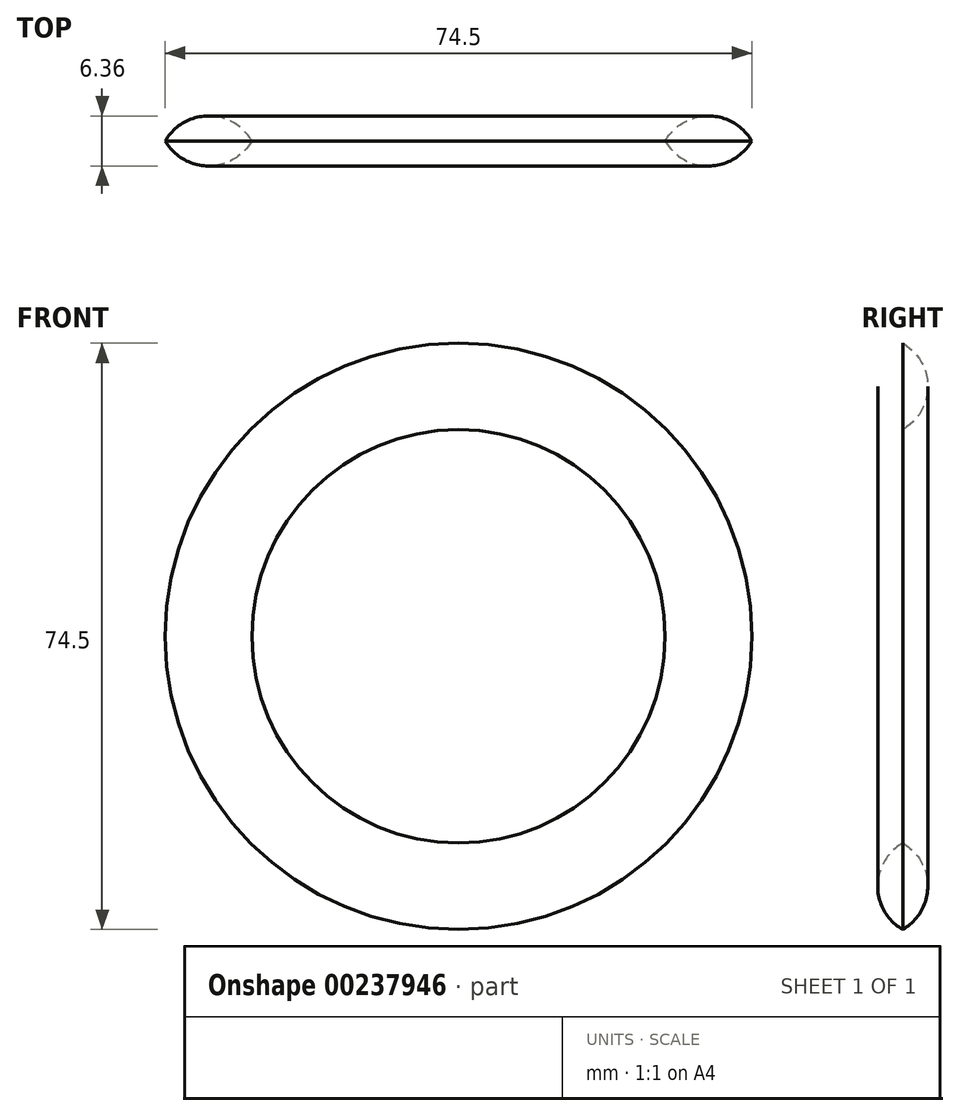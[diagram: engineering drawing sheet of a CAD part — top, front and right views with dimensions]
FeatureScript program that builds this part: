
annotation { "Feature Type Name" : "Feature", "Feature Type Description" : "" }
export const myFeature = defineFeature(function(context is Context, id is Id, definition is map)
    precondition{}
    {
        {
            var Q0;
            Q0=qCreatedBy(makeId("Top.planeOp"),FACE);
            var sketch = newSketch(context, id + "F0", { "sketchPlane" : qUnion([Q0])});
            skLineSegment(sketch, "E0.bottom", {"start": v(6.35, -3.17) * mm, "end": v(-6.35, -3.17) * mm});
            skLineSegment(sketch, "E0.top", {"start": v(6.35, 3.18) * mm, "end": v(-6.35, 3.18) * mm});
            skLineSegment(sketch, "E0.left", {"start": v(6.35, -3.17) * mm, "end": v(6.35, 3.18) * mm});
            skLineSegment(sketch, "E0.right", {"start": v(-6.35, -3.17) * mm, "end": v(-6.35, 3.18) * mm});
            skPoint(sketch, "E0.middle", {"position": v(0, 0) * mm});
            skLineSegment(sketch, "E1", {"start": v(31.75, 34.1) * mm, "end": v(31.75, -34.93) * mm});
            skSolve(sketch);
        }
        {
            var Q0;
            Q0=makeQuery(id+"F0.imprint","IMPRINT",FACE,{"disambiguationData":[TD([[makeQuery(id+"F0.imprint","IMPRINT",EDGE,{"derivedFrom":sQuery(id+"F0.wireOp",EDGE,"E0.bottom")}),-1.0]])]});
            var Q1;
            Q1=sQuery(id+"F0.wireOp",EDGE,"E1");
            revolve(context, id + "F1", {"entities" : qUnion([Q0]), "axis" : qUnion([Q1]), "revolveType" : RevolveType.FULL});
        }
        {
            var Q0;
            Q0=makeQuery(id+"F1.opRevolve","SWEPT_EDGE",EDGE,{"disambiguationData":[OSD([sQuery(id+"F0.wireOp",EDGE,"E0.top"),sQuery(id+"F0.wireOp",EDGE,"E0.left")])]});
            fillet(context, id + "F2", {"entities" : qUnion([Q0]), "radius" : 6.35 * mm, "tangentPropagation" : true, "allowEdgeOverflow" : false});
        }
        {
            var Q0;
            Q0=makeQuery(id+"F1.opRevolve","SWEPT_EDGE",EDGE,{"disambiguationData":[OSD([sQuery(id+"F0.wireOp",EDGE,"E0.top"),sQuery(id+"F0.wireOp",EDGE,"E0.right")])]});
            fillet(context, id + "F3", {"entities" : qUnion([Q0]), "radius" : 6.35 * mm, "tangentPropagation" : true, "allowEdgeOverflow" : false});
        }
        {
            var Q0;
            Q0=makeQuery(id+"F1.opRevolve","SWEPT_BODY",BODY,{"disambiguationData":[OSD([sQuery(id+"F0.wireOp",EDGE,"E0.bottom"),sQuery(id+"F0.wireOp",EDGE,"E0.top"),sQuery(id+"F0.wireOp",EDGE,"E0.left"),sQuery(id+"F0.wireOp",EDGE,"E0.right")])]});
            var Q1;
            Q1=qCreatedBy(makeId("Front.planeOp"),FACE);
            mirror(context, id + "F4", {"operationType" : NewBodyOperationType.INTERSECT, "entities" : qUnion([Q0]), "mirrorPlane" : qUnion([Q1])});
        }
    });
